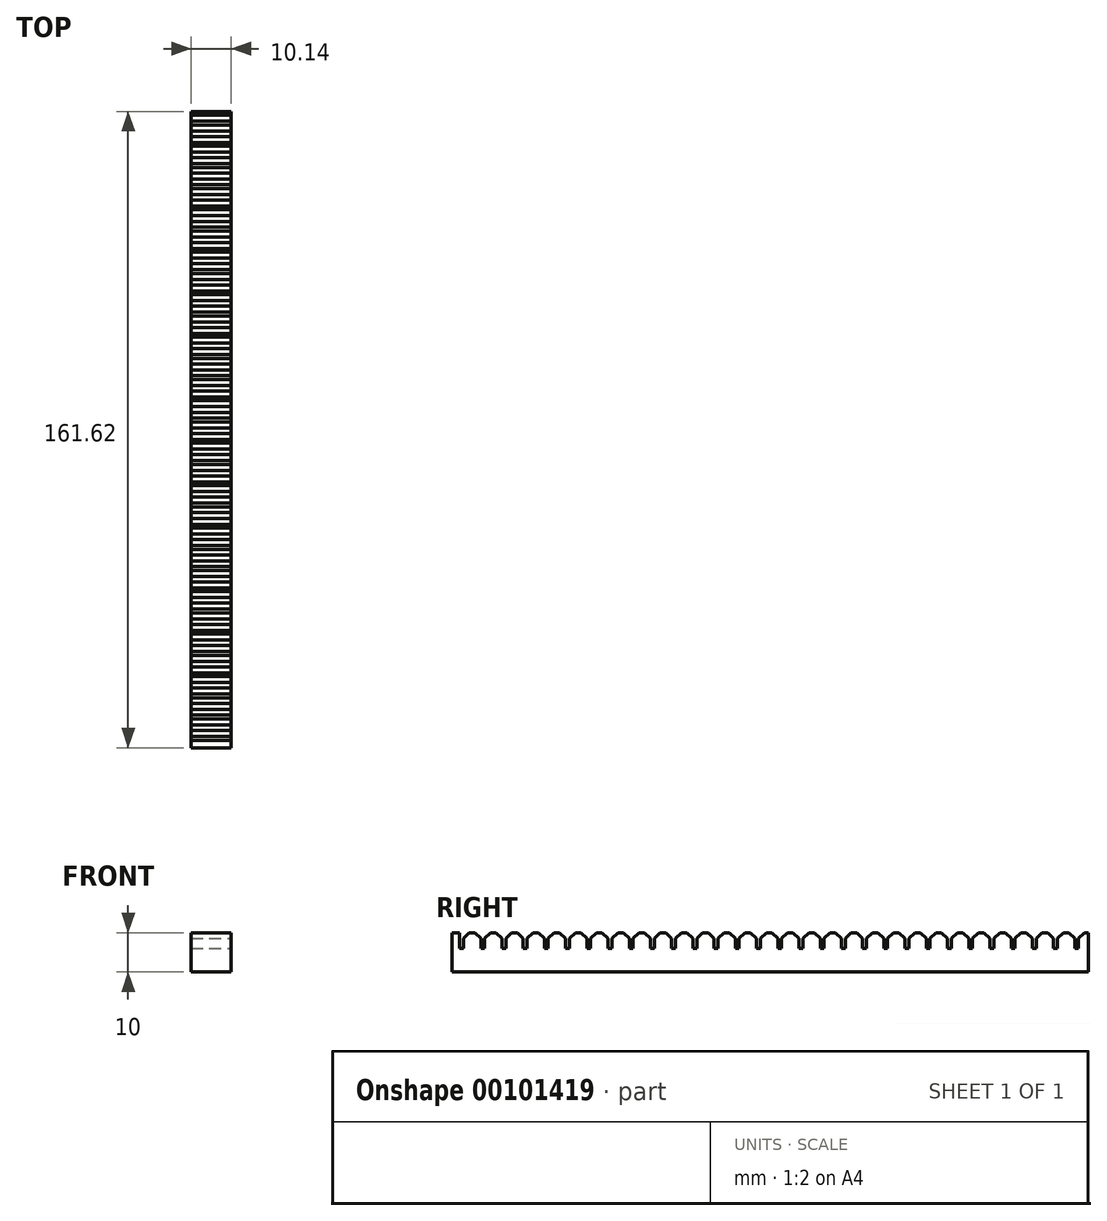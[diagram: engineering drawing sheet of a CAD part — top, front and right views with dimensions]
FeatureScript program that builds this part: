
annotation { "Feature Type Name" : "Feature", "Feature Type Description" : "" }
export const myFeature = defineFeature(function(context is Context, id is Id, definition is map)
    precondition{}
    {
        {
            var Q0;
            Q0=qCreatedBy(makeId("Top.planeOp"),FACE);
            var sketch = newSketch(context, id + "F0", { "sketchPlane" : qUnion([Q0])});
            skLineSegment(sketch, "E0.bottom", {"start": v(5.07, 80.81) * mm, "end": v(-5.07, 80.81) * mm});
            skLineSegment(sketch, "E0.top", {"start": v(5.07, -80.81) * mm, "end": v(-5.07, -80.81) * mm});
            skLineSegment(sketch, "E0.left", {"start": v(5.07, 80.81) * mm, "end": v(5.07, -80.81) * mm});
            skLineSegment(sketch, "E0.right", {"start": v(-5.07, 80.81) * mm, "end": v(-5.07, -80.81) * mm});
            skPoint(sketch, "E0.middle", {"position": v(0, 0) * mm});
            skSolve(sketch);
        }
        {
            var Q0;
            Q0=makeQuery(id+"F0.imprint","IMPRINT",FACE,{"disambiguationData":[TD([[makeQuery(id+"F0.imprint","IMPRINT",EDGE,{"derivedFrom":sQuery(id+"F0.wireOp",EDGE,"E0.bottom")}),1.0]])]});
            extrude(context, id + "F1", {"entities" : qUnion([Q0]), "depth" : 10 * mm});
        }
        {
            var Q0;
            Q0=makeQuery(id+"F1.opExtrude","CAP_FACE",FACE,{"disambiguationData":[OSD([sQuery(id+"F0.wireOp",EDGE,"E0.bottom"),sQuery(id+"F0.wireOp",EDGE,"E0.top"),sQuery(id+"F0.wireOp",EDGE,"E0.left"),sQuery(id+"F0.wireOp",EDGE,"E0.right")])],"isStart":false});
            var sketch = newSketch(context, id + "F2", { "sketchPlane" : qUnion([Q0])});
            skLineSegment(sketch, "E1.bottom", {"start": v(-5.07, -78.9) * mm, "end": v(5.07, -78.9) * mm});
            skLineSegment(sketch, "E1.top", {"start": v(-5.07, -77.94) * mm, "end": v(5.07, -77.94) * mm});
            skLineSegment(sketch, "E1.left", {"start": v(-5.07, -78.9) * mm, "end": v(-5.07, -77.94) * mm});
            skLineSegment(sketch, "E1.right", {"start": v(5.07, -78.9) * mm, "end": v(5.07, -77.94) * mm});
            skLineSegment(sketch, "E2.0.1.0", {"start": v(-5.07, -73.51) * mm, "end": v(5.07, -73.51) * mm});
            skLineSegment(sketch, "E2.0.1.1", {"start": v(-5.07, -72.55) * mm, "end": v(5.07, -72.55) * mm});
            skLineSegment(sketch, "E2.0.1.2", {"start": v(-5.07, -73.51) * mm, "end": v(-5.07, -72.55) * mm});
            skLineSegment(sketch, "E2.0.1.3", {"start": v(5.07, -73.51) * mm, "end": v(5.07, -72.55) * mm});
            skLineSegment(sketch, "E2.0.2.0", {"start": v(-5.07, -68.12) * mm, "end": v(5.07, -68.12) * mm});
            skLineSegment(sketch, "E2.0.2.1", {"start": v(-5.07, -67.16) * mm, "end": v(5.07, -67.16) * mm});
            skLineSegment(sketch, "E2.0.2.2", {"start": v(-5.07, -68.12) * mm, "end": v(-5.07, -67.16) * mm});
            skLineSegment(sketch, "E2.0.2.3", {"start": v(5.07, -68.12) * mm, "end": v(5.07, -67.16) * mm});
            skLineSegment(sketch, "E2.0.3.0", {"start": v(-5.07, -62.73) * mm, "end": v(5.07, -62.73) * mm});
            skLineSegment(sketch, "E2.0.3.1", {"start": v(-5.07, -61.77) * mm, "end": v(5.07, -61.77) * mm});
            skLineSegment(sketch, "E2.0.3.2", {"start": v(-5.07, -62.73) * mm, "end": v(-5.07, -61.77) * mm});
            skLineSegment(sketch, "E2.0.3.3", {"start": v(5.07, -62.73) * mm, "end": v(5.07, -61.77) * mm});
            skLineSegment(sketch, "E2.0.4.0", {"start": v(-5.07, -57.34) * mm, "end": v(5.07, -57.34) * mm});
            skLineSegment(sketch, "E2.0.4.1", {"start": v(-5.07, -56.38) * mm, "end": v(5.07, -56.38) * mm});
            skLineSegment(sketch, "E2.0.4.2", {"start": v(-5.07, -57.34) * mm, "end": v(-5.07, -56.38) * mm});
            skLineSegment(sketch, "E2.0.4.3", {"start": v(5.07, -57.34) * mm, "end": v(5.07, -56.38) * mm});
            skLineSegment(sketch, "E2.0.5.0", {"start": v(-5.07, -51.95) * mm, "end": v(5.07, -51.95) * mm});
            skLineSegment(sketch, "E2.0.5.1", {"start": v(-5.07, -50.99) * mm, "end": v(5.07, -50.99) * mm});
            skLineSegment(sketch, "E2.0.5.2", {"start": v(-5.07, -51.95) * mm, "end": v(-5.07, -50.99) * mm});
            skLineSegment(sketch, "E2.0.5.3", {"start": v(5.07, -51.95) * mm, "end": v(5.07, -50.99) * mm});
            skLineSegment(sketch, "E2.0.6.0", {"start": v(-5.07, -46.56) * mm, "end": v(5.07, -46.56) * mm});
            skLineSegment(sketch, "E2.0.6.1", {"start": v(-5.07, -45.6) * mm, "end": v(5.07, -45.6) * mm});
            skLineSegment(sketch, "E2.0.6.2", {"start": v(-5.07, -46.56) * mm, "end": v(-5.07, -45.6) * mm});
            skLineSegment(sketch, "E2.0.6.3", {"start": v(5.07, -46.56) * mm, "end": v(5.07, -45.6) * mm});
            skLineSegment(sketch, "E2.0.7.0", {"start": v(-5.07, -41.17) * mm, "end": v(5.07, -41.17) * mm});
            skLineSegment(sketch, "E2.0.7.1", {"start": v(-5.07, -40.2) * mm, "end": v(5.07, -40.2) * mm});
            skLineSegment(sketch, "E2.0.7.2", {"start": v(-5.07, -41.17) * mm, "end": v(-5.07, -40.2) * mm});
            skLineSegment(sketch, "E2.0.7.3", {"start": v(5.07, -41.17) * mm, "end": v(5.07, -40.2) * mm});
            skLineSegment(sketch, "E2.0.8.0", {"start": v(-5.07, -35.78) * mm, "end": v(5.07, -35.78) * mm});
            skLineSegment(sketch, "E2.0.8.1", {"start": v(-5.07, -34.82) * mm, "end": v(5.07, -34.82) * mm});
            skLineSegment(sketch, "E2.0.8.2", {"start": v(-5.07, -35.78) * mm, "end": v(-5.07, -34.82) * mm});
            skLineSegment(sketch, "E2.0.8.3", {"start": v(5.07, -35.78) * mm, "end": v(5.07, -34.82) * mm});
            skLineSegment(sketch, "E2.0.9.0", {"start": v(-5.07, -30.4) * mm, "end": v(5.07, -30.4) * mm});
            skLineSegment(sketch, "E2.0.9.1", {"start": v(-5.07, -29.43) * mm, "end": v(5.07, -29.43) * mm});
            skLineSegment(sketch, "E2.0.9.2", {"start": v(-5.07, -30.4) * mm, "end": v(-5.07, -29.43) * mm});
            skLineSegment(sketch, "E2.0.9.3", {"start": v(5.07, -30.4) * mm, "end": v(5.07, -29.43) * mm});
            skLineSegment(sketch, "E2.0.10.0", {"start": v(-5.07, -25) * mm, "end": v(5.07, -25) * mm});
            skLineSegment(sketch, "E2.0.10.1", {"start": v(-5.07, -24.04) * mm, "end": v(5.07, -24.04) * mm});
            skLineSegment(sketch, "E2.0.10.2", {"start": v(-5.07, -25) * mm, "end": v(-5.07, -24.04) * mm});
            skLineSegment(sketch, "E2.0.10.3", {"start": v(5.07, -25) * mm, "end": v(5.07, -24.04) * mm});
            skLineSegment(sketch, "E2.0.11.0", {"start": v(-5.07, -19.61) * mm, "end": v(5.07, -19.61) * mm});
            skLineSegment(sketch, "E2.0.11.1", {"start": v(-5.07, -18.65) * mm, "end": v(5.07, -18.65) * mm});
            skLineSegment(sketch, "E2.0.11.2", {"start": v(-5.07, -19.61) * mm, "end": v(-5.07, -18.65) * mm});
            skLineSegment(sketch, "E2.0.11.3", {"start": v(5.07, -19.61) * mm, "end": v(5.07, -18.65) * mm});
            skLineSegment(sketch, "E2.0.12.0", {"start": v(-5.07, -14.22) * mm, "end": v(5.07, -14.22) * mm});
            skLineSegment(sketch, "E2.0.12.1", {"start": v(-5.07, -13.26) * mm, "end": v(5.07, -13.26) * mm});
            skLineSegment(sketch, "E2.0.12.2", {"start": v(-5.07, -14.22) * mm, "end": v(-5.07, -13.26) * mm});
            skLineSegment(sketch, "E2.0.12.3", {"start": v(5.07, -14.22) * mm, "end": v(5.07, -13.26) * mm});
            skLineSegment(sketch, "E2.0.13.0", {"start": v(-5.07, -8.83) * mm, "end": v(5.07, -8.83) * mm});
            skLineSegment(sketch, "E2.0.13.1", {"start": v(-5.07, -7.87) * mm, "end": v(5.07, -7.87) * mm});
            skLineSegment(sketch, "E2.0.13.2", {"start": v(-5.07, -8.83) * mm, "end": v(-5.07, -7.87) * mm});
            skLineSegment(sketch, "E2.0.13.3", {"start": v(5.07, -8.83) * mm, "end": v(5.07, -7.87) * mm});
            skLineSegment(sketch, "E2.0.14.0", {"start": v(-5.07, -3.44) * mm, "end": v(5.07, -3.44) * mm});
            skLineSegment(sketch, "E2.0.14.1", {"start": v(-5.07, -2.48) * mm, "end": v(5.07, -2.48) * mm});
            skLineSegment(sketch, "E2.0.14.2", {"start": v(-5.07, -3.44) * mm, "end": v(-5.07, -2.48) * mm});
            skLineSegment(sketch, "E2.0.14.3", {"start": v(5.07, -3.44) * mm, "end": v(5.07, -2.48) * mm});
            skLineSegment(sketch, "E2.0.15.0", {"start": v(-5.07, 1.95) * mm, "end": v(5.07, 1.95) * mm});
            skLineSegment(sketch, "E2.0.15.1", {"start": v(-5.07, 2.91) * mm, "end": v(5.07, 2.91) * mm});
            skLineSegment(sketch, "E2.0.15.2", {"start": v(-5.07, 1.95) * mm, "end": v(-5.07, 2.91) * mm});
            skLineSegment(sketch, "E2.0.15.3", {"start": v(5.07, 1.95) * mm, "end": v(5.07, 2.91) * mm});
            skLineSegment(sketch, "E2.0.16.0", {"start": v(-5.07, 7.34) * mm, "end": v(5.07, 7.34) * mm});
            skLineSegment(sketch, "E2.0.16.1", {"start": v(-5.07, 8.3) * mm, "end": v(5.07, 8.3) * mm});
            skLineSegment(sketch, "E2.0.16.2", {"start": v(-5.07, 7.34) * mm, "end": v(-5.07, 8.3) * mm});
            skLineSegment(sketch, "E2.0.16.3", {"start": v(5.07, 7.34) * mm, "end": v(5.07, 8.3) * mm});
            skLineSegment(sketch, "E2.0.17.0", {"start": v(-5.07, 12.73) * mm, "end": v(5.07, 12.73) * mm});
            skLineSegment(sketch, "E2.0.17.1", {"start": v(-5.07, 13.7) * mm, "end": v(5.07, 13.7) * mm});
            skLineSegment(sketch, "E2.0.17.2", {"start": v(-5.07, 12.73) * mm, "end": v(-5.07, 13.7) * mm});
            skLineSegment(sketch, "E2.0.17.3", {"start": v(5.07, 12.73) * mm, "end": v(5.07, 13.7) * mm});
            skLineSegment(sketch, "E2.0.18.0", {"start": v(-5.07, 18.12) * mm, "end": v(5.07, 18.12) * mm});
            skLineSegment(sketch, "E2.0.18.1", {"start": v(-5.07, 19.08) * mm, "end": v(5.07, 19.08) * mm});
            skLineSegment(sketch, "E2.0.18.2", {"start": v(-5.07, 18.12) * mm, "end": v(-5.07, 19.08) * mm});
            skLineSegment(sketch, "E2.0.18.3", {"start": v(5.07, 18.12) * mm, "end": v(5.07, 19.08) * mm});
            skLineSegment(sketch, "E2.0.19.0", {"start": v(-5.07, 23.5) * mm, "end": v(5.07, 23.5) * mm});
            skLineSegment(sketch, "E2.0.19.1", {"start": v(-5.07, 24.47) * mm, "end": v(5.07, 24.47) * mm});
            skLineSegment(sketch, "E2.0.19.2", {"start": v(-5.07, 23.5) * mm, "end": v(-5.07, 24.47) * mm});
            skLineSegment(sketch, "E2.0.19.3", {"start": v(5.07, 23.5) * mm, "end": v(5.07, 24.47) * mm});
            skLineSegment(sketch, "E2.0.20.0", {"start": v(-5.07, 28.9) * mm, "end": v(5.07, 28.9) * mm});
            skLineSegment(sketch, "E2.0.20.1", {"start": v(-5.07, 29.86) * mm, "end": v(5.07, 29.86) * mm});
            skLineSegment(sketch, "E2.0.20.2", {"start": v(-5.07, 28.9) * mm, "end": v(-5.07, 29.86) * mm});
            skLineSegment(sketch, "E2.0.20.3", {"start": v(5.07, 28.9) * mm, "end": v(5.07, 29.86) * mm});
            skLineSegment(sketch, "E2.0.21.0", {"start": v(-5.07, 34.29) * mm, "end": v(5.07, 34.29) * mm});
            skLineSegment(sketch, "E2.0.21.1", {"start": v(-5.07, 35.25) * mm, "end": v(5.07, 35.25) * mm});
            skLineSegment(sketch, "E2.0.21.2", {"start": v(-5.07, 34.29) * mm, "end": v(-5.07, 35.25) * mm});
            skLineSegment(sketch, "E2.0.21.3", {"start": v(5.07, 34.29) * mm, "end": v(5.07, 35.25) * mm});
            skLineSegment(sketch, "E2.0.22.0", {"start": v(-5.07, 39.68) * mm, "end": v(5.07, 39.68) * mm});
            skLineSegment(sketch, "E2.0.22.1", {"start": v(-5.07, 40.64) * mm, "end": v(5.07, 40.64) * mm});
            skLineSegment(sketch, "E2.0.22.2", {"start": v(-5.07, 39.68) * mm, "end": v(-5.07, 40.64) * mm});
            skLineSegment(sketch, "E2.0.22.3", {"start": v(5.07, 39.68) * mm, "end": v(5.07, 40.64) * mm});
            skLineSegment(sketch, "E2.0.23.0", {"start": v(-5.07, 45.07) * mm, "end": v(5.07, 45.07) * mm});
            skLineSegment(sketch, "E2.0.23.1", {"start": v(-5.07, 46.03) * mm, "end": v(5.07, 46.03) * mm});
            skLineSegment(sketch, "E2.0.23.2", {"start": v(-5.07, 45.07) * mm, "end": v(-5.07, 46.03) * mm});
            skLineSegment(sketch, "E2.0.23.3", {"start": v(5.07, 45.07) * mm, "end": v(5.07, 46.03) * mm});
            skLineSegment(sketch, "E2.0.24.0", {"start": v(-5.07, 50.46) * mm, "end": v(5.07, 50.46) * mm});
            skLineSegment(sketch, "E2.0.24.1", {"start": v(-5.07, 51.42) * mm, "end": v(5.07, 51.42) * mm});
            skLineSegment(sketch, "E2.0.24.2", {"start": v(-5.07, 50.46) * mm, "end": v(-5.07, 51.42) * mm});
            skLineSegment(sketch, "E2.0.24.3", {"start": v(5.07, 50.46) * mm, "end": v(5.07, 51.42) * mm});
            skLineSegment(sketch, "E2.0.25.0", {"start": v(-5.07, 55.85) * mm, "end": v(5.07, 55.85) * mm});
            skLineSegment(sketch, "E2.0.25.1", {"start": v(-5.07, 56.81) * mm, "end": v(5.07, 56.81) * mm});
            skLineSegment(sketch, "E2.0.25.2", {"start": v(-5.07, 55.85) * mm, "end": v(-5.07, 56.81) * mm});
            skLineSegment(sketch, "E2.0.25.3", {"start": v(5.07, 55.85) * mm, "end": v(5.07, 56.81) * mm});
            skLineSegment(sketch, "E2.0.26.0", {"start": v(-5.07, 61.24) * mm, "end": v(5.07, 61.24) * mm});
            skLineSegment(sketch, "E2.0.26.1", {"start": v(-5.07, 62.2) * mm, "end": v(5.07, 62.2) * mm});
            skLineSegment(sketch, "E2.0.26.2", {"start": v(-5.07, 61.24) * mm, "end": v(-5.07, 62.2) * mm});
            skLineSegment(sketch, "E2.0.26.3", {"start": v(5.07, 61.24) * mm, "end": v(5.07, 62.2) * mm});
            skLineSegment(sketch, "E2.0.27.0", {"start": v(-5.07, 66.63) * mm, "end": v(5.07, 66.63) * mm});
            skLineSegment(sketch, "E2.0.27.1", {"start": v(-5.07, 67.6) * mm, "end": v(5.07, 67.6) * mm});
            skLineSegment(sketch, "E2.0.27.2", {"start": v(-5.07, 66.63) * mm, "end": v(-5.07, 67.6) * mm});
            skLineSegment(sketch, "E2.0.27.3", {"start": v(5.07, 66.63) * mm, "end": v(5.07, 67.6) * mm});
            skLineSegment(sketch, "E2.0.28.0", {"start": v(-5.07, 72.02) * mm, "end": v(5.07, 72.02) * mm});
            skLineSegment(sketch, "E2.0.28.1", {"start": v(-5.07, 72.98) * mm, "end": v(5.07, 72.98) * mm});
            skLineSegment(sketch, "E2.0.28.2", {"start": v(-5.07, 72.02) * mm, "end": v(-5.07, 72.98) * mm});
            skLineSegment(sketch, "E2.0.28.3", {"start": v(5.07, 72.02) * mm, "end": v(5.07, 72.98) * mm});
            skLineSegment(sketch, "E2.0.29.0", {"start": v(-5.07, 77.4) * mm, "end": v(5.07, 77.4) * mm});
            skLineSegment(sketch, "E2.0.29.1", {"start": v(-5.07, 78.37) * mm, "end": v(5.07, 78.37) * mm});
            skLineSegment(sketch, "E2.0.29.2", {"start": v(-5.07, 77.4) * mm, "end": v(-5.07, 78.37) * mm});
            skLineSegment(sketch, "E2.0.29.3", {"start": v(5.07, 77.4) * mm, "end": v(5.07, 78.37) * mm});
            skLineSegment(sketch, "E2.direction1", {"start": v(-5.07, -76.25) * mm, "end": v(19.93, -76.25) * mm, "construction": true});
            skLineSegment(sketch, "E2.direction2", {"start": v(-5.07, -78.9) * mm, "end": v(-5.07, -73.51) * mm, "construction": true});
            skSolve(sketch);
        }
        {
            var Q0;
            Q0=makeQuery(id+"F2.imprint","IMPRINT",FACE,{"disambiguationData":[TD([[makeQuery(id+"F2.imprint","IMPRINT",EDGE,{"derivedFrom":sQuery(id+"F2.wireOp",EDGE,"E1.bottom")}),1.0]])]});
            var Q1;
            Q1=makeQuery(id+"F2.imprint","IMPRINT",FACE,{"disambiguationData":[TD([[makeQuery(id+"F2.imprint","IMPRINT",EDGE,{"derivedFrom":sQuery(id+"F2.wireOp",EDGE,"E2.0.1.0")}),1.0]])]});
            var Q2;
            Q2=makeQuery(id+"F2.imprint","IMPRINT",FACE,{"disambiguationData":[TD([[makeQuery(id+"F2.imprint","IMPRINT",EDGE,{"derivedFrom":sQuery(id+"F2.wireOp",EDGE,"E2.0.2.0")}),1.0]])]});
            var Q3;
            Q3=makeQuery(id+"F2.imprint","IMPRINT",FACE,{"disambiguationData":[TD([[makeQuery(id+"F2.imprint","IMPRINT",EDGE,{"derivedFrom":sQuery(id+"F2.wireOp",EDGE,"E2.0.3.0")}),1.0]])]});
            var Q4;
            Q4=makeQuery(id+"F2.imprint","IMPRINT",FACE,{"disambiguationData":[TD([[makeQuery(id+"F2.imprint","IMPRINT",EDGE,{"derivedFrom":sQuery(id+"F2.wireOp",EDGE,"E2.0.4.0")}),1.0]])]});
            var Q5;
            Q5=makeQuery(id+"F2.imprint","IMPRINT",FACE,{"disambiguationData":[TD([[makeQuery(id+"F2.imprint","IMPRINT",EDGE,{"derivedFrom":sQuery(id+"F2.wireOp",EDGE,"E2.0.5.0")}),1.0]])]});
            var Q6;
            Q6=makeQuery(id+"F2.imprint","IMPRINT",FACE,{"disambiguationData":[TD([[makeQuery(id+"F2.imprint","IMPRINT",EDGE,{"derivedFrom":sQuery(id+"F2.wireOp",EDGE,"E2.0.6.0")}),1.0]])]});
            var Q7;
            Q7=makeQuery(id+"F2.imprint","IMPRINT",FACE,{"disambiguationData":[TD([[makeQuery(id+"F2.imprint","IMPRINT",EDGE,{"derivedFrom":sQuery(id+"F2.wireOp",EDGE,"E2.0.7.0")}),1.0]])]});
            var Q8;
            Q8=makeQuery(id+"F2.imprint","IMPRINT",FACE,{"disambiguationData":[TD([[makeQuery(id+"F2.imprint","IMPRINT",EDGE,{"derivedFrom":sQuery(id+"F2.wireOp",EDGE,"E2.0.8.0")}),1.0]])]});
            var Q9;
            Q9=makeQuery(id+"F2.imprint","IMPRINT",FACE,{"disambiguationData":[TD([[makeQuery(id+"F2.imprint","IMPRINT",EDGE,{"derivedFrom":sQuery(id+"F2.wireOp",EDGE,"E2.0.9.0")}),1.0]])]});
            var Q10;
            Q10=makeQuery(id+"F2.imprint","IMPRINT",FACE,{"disambiguationData":[TD([[makeQuery(id+"F2.imprint","IMPRINT",EDGE,{"derivedFrom":sQuery(id+"F2.wireOp",EDGE,"E2.0.10.0")}),1.0]])]});
            var Q11;
            Q11=makeQuery(id+"F2.imprint","IMPRINT",FACE,{"disambiguationData":[TD([[makeQuery(id+"F2.imprint","IMPRINT",EDGE,{"derivedFrom":sQuery(id+"F2.wireOp",EDGE,"E2.0.11.0")}),1.0]])]});
            var Q12;
            Q12=makeQuery(id+"F2.imprint","IMPRINT",FACE,{"disambiguationData":[TD([[makeQuery(id+"F2.imprint","IMPRINT",EDGE,{"derivedFrom":sQuery(id+"F2.wireOp",EDGE,"E2.0.12.0")}),1.0]])]});
            var Q13;
            Q13=makeQuery(id+"F2.imprint","IMPRINT",FACE,{"disambiguationData":[TD([[makeQuery(id+"F2.imprint","IMPRINT",EDGE,{"derivedFrom":sQuery(id+"F2.wireOp",EDGE,"E2.0.13.0")}),1.0]])]});
            var Q14;
            Q14=makeQuery(id+"F2.imprint","IMPRINT",FACE,{"disambiguationData":[TD([[makeQuery(id+"F2.imprint","IMPRINT",EDGE,{"derivedFrom":sQuery(id+"F2.wireOp",EDGE,"E2.0.14.0")}),1.0]])]});
            var Q15;
            Q15=makeQuery(id+"F2.imprint","IMPRINT",FACE,{"disambiguationData":[TD([[makeQuery(id+"F2.imprint","IMPRINT",EDGE,{"derivedFrom":sQuery(id+"F2.wireOp",EDGE,"E2.0.15.0")}),1.0]])]});
            var Q16;
            Q16=makeQuery(id+"F2.imprint","IMPRINT",FACE,{"disambiguationData":[TD([[makeQuery(id+"F2.imprint","IMPRINT",EDGE,{"derivedFrom":sQuery(id+"F2.wireOp",EDGE,"E2.0.16.0")}),1.0]])]});
            var Q17;
            Q17=makeQuery(id+"F2.imprint","IMPRINT",FACE,{"disambiguationData":[TD([[makeQuery(id+"F2.imprint","IMPRINT",EDGE,{"derivedFrom":sQuery(id+"F2.wireOp",EDGE,"E2.0.17.0")}),1.0]])]});
            var Q18;
            Q18=makeQuery(id+"F2.imprint","IMPRINT",FACE,{"disambiguationData":[TD([[makeQuery(id+"F2.imprint","IMPRINT",EDGE,{"derivedFrom":sQuery(id+"F2.wireOp",EDGE,"E2.0.18.0")}),1.0]])]});
            var Q19;
            Q19=makeQuery(id+"F2.imprint","IMPRINT",FACE,{"disambiguationData":[TD([[makeQuery(id+"F2.imprint","IMPRINT",EDGE,{"derivedFrom":sQuery(id+"F2.wireOp",EDGE,"E2.0.19.0")}),1.0]])]});
            var Q20;
            Q20=makeQuery(id+"F2.imprint","IMPRINT",FACE,{"disambiguationData":[TD([[makeQuery(id+"F2.imprint","IMPRINT",EDGE,{"derivedFrom":sQuery(id+"F2.wireOp",EDGE,"E2.0.20.0")}),1.0]])]});
            var Q21;
            Q21=makeQuery(id+"F2.imprint","IMPRINT",FACE,{"disambiguationData":[TD([[makeQuery(id+"F2.imprint","IMPRINT",EDGE,{"derivedFrom":sQuery(id+"F2.wireOp",EDGE,"E2.0.21.0")}),1.0]])]});
            var Q22;
            Q22=makeQuery(id+"F2.imprint","IMPRINT",FACE,{"disambiguationData":[TD([[makeQuery(id+"F2.imprint","IMPRINT",EDGE,{"derivedFrom":sQuery(id+"F2.wireOp",EDGE,"E2.0.22.0")}),1.0]])]});
            var Q23;
            Q23=makeQuery(id+"F2.imprint","IMPRINT",FACE,{"disambiguationData":[TD([[makeQuery(id+"F2.imprint","IMPRINT",EDGE,{"derivedFrom":sQuery(id+"F2.wireOp",EDGE,"E2.0.23.0")}),1.0]])]});
            var Q24;
            Q24=makeQuery(id+"F2.imprint","IMPRINT",FACE,{"disambiguationData":[TD([[makeQuery(id+"F2.imprint","IMPRINT",EDGE,{"derivedFrom":sQuery(id+"F2.wireOp",EDGE,"E2.0.24.0")}),1.0]])]});
            var Q25;
            Q25=makeQuery(id+"F2.imprint","IMPRINT",FACE,{"disambiguationData":[TD([[makeQuery(id+"F2.imprint","IMPRINT",EDGE,{"derivedFrom":sQuery(id+"F2.wireOp",EDGE,"E2.0.25.0")}),1.0]])]});
            var Q26;
            Q26=makeQuery(id+"F2.imprint","IMPRINT",FACE,{"disambiguationData":[TD([[makeQuery(id+"F2.imprint","IMPRINT",EDGE,{"derivedFrom":sQuery(id+"F2.wireOp",EDGE,"E2.0.26.0")}),1.0]])]});
            var Q27;
            Q27=makeQuery(id+"F2.imprint","IMPRINT",FACE,{"disambiguationData":[TD([[makeQuery(id+"F2.imprint","IMPRINT",EDGE,{"derivedFrom":sQuery(id+"F2.wireOp",EDGE,"E2.0.27.0")}),1.0]])]});
            var Q28;
            Q28=makeQuery(id+"F2.imprint","IMPRINT",FACE,{"disambiguationData":[TD([[makeQuery(id+"F2.imprint","IMPRINT",EDGE,{"derivedFrom":sQuery(id+"F2.wireOp",EDGE,"E2.0.28.0")}),1.0]])]});
            var Q29;
            Q29=makeQuery(id+"F2.imprint","IMPRINT",FACE,{"disambiguationData":[TD([[makeQuery(id+"F2.imprint","IMPRINT",EDGE,{"derivedFrom":sQuery(id+"F2.wireOp",EDGE,"E2.0.29.0")}),1.0]])]});
            extrude(context, id + "F3", {"entities" : qUnion([Q0, Q1, Q2, Q3, Q4, Q5, Q6, Q7, Q8, Q9, Q10, Q11, Q12, Q13, Q14, Q15, Q16, Q17, Q18, Q19, Q20, Q21, Q22, Q23, Q24, Q25, Q26, Q27, Q28, Q29]), "operationType" : NewBodyOperationType.REMOVE, "oppositeDirection" : true, "depth" : 4 * mm});
        }
        {
            var Q0;
            Q0=makeQuery(id+"F3.boolean.opBoolean","COPY",EDGE,{"derivedFrom":makeQuery(id+"F3.opExtrude","CAP_EDGE",EDGE,{"disambiguationData":[OSD([sQuery(id+"F2.wireOp",EDGE,"E2.0.5.1")])],"isStart":true})});
            var Q1;
            Q1=makeQuery(id+"F3.boolean.opBoolean","COPY",EDGE,{"derivedFrom":makeQuery(id+"F3.opExtrude","CAP_EDGE",EDGE,{"disambiguationData":[OSD([sQuery(id+"F2.wireOp",EDGE,"E2.0.5.0")])],"isStart":true})});
            var Q2;
            Q2=makeQuery(id+"F3.boolean.opBoolean","COPY",EDGE,{"derivedFrom":makeQuery(id+"F3.opExtrude","CAP_EDGE",EDGE,{"disambiguationData":[OSD([sQuery(id+"F2.wireOp",EDGE,"E2.0.4.0")])],"isStart":true})});
            var Q3;
            Q3=makeQuery(id+"F3.boolean.opBoolean","COPY",EDGE,{"derivedFrom":makeQuery(id+"F3.opExtrude","CAP_EDGE",EDGE,{"disambiguationData":[OSD([sQuery(id+"F2.wireOp",EDGE,"E2.0.4.1")])],"isStart":true})});
            var Q4;
            Q4=makeQuery(id+"F3.boolean.opBoolean","COPY",EDGE,{"derivedFrom":makeQuery(id+"F3.opExtrude","CAP_EDGE",EDGE,{"disambiguationData":[OSD([sQuery(id+"F2.wireOp",EDGE,"E2.0.3.1")])],"isStart":true})});
            var Q5;
            Q5=makeQuery(id+"F3.boolean.opBoolean","COPY",EDGE,{"derivedFrom":makeQuery(id+"F3.opExtrude","CAP_EDGE",EDGE,{"disambiguationData":[OSD([sQuery(id+"F2.wireOp",EDGE,"E2.0.3.0")])],"isStart":true})});
            var Q6;
            Q6=makeQuery(id+"F3.boolean.opBoolean","COPY",EDGE,{"derivedFrom":makeQuery(id+"F3.opExtrude","CAP_EDGE",EDGE,{"disambiguationData":[OSD([sQuery(id+"F2.wireOp",EDGE,"E2.0.2.1")])],"isStart":true})});
            var Q7;
            Q7=makeQuery(id+"F3.boolean.opBoolean","COPY",EDGE,{"derivedFrom":makeQuery(id+"F3.opExtrude","CAP_EDGE",EDGE,{"disambiguationData":[OSD([sQuery(id+"F2.wireOp",EDGE,"E2.0.2.0")])],"isStart":true})});
            var Q8;
            Q8=makeQuery(id+"F3.boolean.opBoolean","COPY",EDGE,{"derivedFrom":makeQuery(id+"F3.opExtrude","CAP_EDGE",EDGE,{"disambiguationData":[OSD([sQuery(id+"F2.wireOp",EDGE,"E2.0.1.1")])],"isStart":true})});
            var Q9;
            Q9=makeQuery(id+"F3.boolean.opBoolean","COPY",EDGE,{"derivedFrom":makeQuery(id+"F3.opExtrude","CAP_EDGE",EDGE,{"disambiguationData":[OSD([sQuery(id+"F2.wireOp",EDGE,"E2.0.1.0")])],"isStart":true})});
            var Q10;
            Q10=makeQuery(id+"F3.boolean.opBoolean","COPY",EDGE,{"derivedFrom":makeQuery(id+"F3.opExtrude","CAP_EDGE",EDGE,{"disambiguationData":[OSD([sQuery(id+"F2.wireOp",EDGE,"E1.top")])],"isStart":true})});
            var Q11;
            Q11=makeQuery(id+"F3.boolean.opBoolean","COPY",EDGE,{"derivedFrom":makeQuery(id+"F3.opExtrude","CAP_EDGE",EDGE,{"disambiguationData":[OSD([sQuery(id+"F2.wireOp",EDGE,"E1.bottom")])],"isStart":true})});
            var Q12;
            Q12=makeQuery(id+"F3.boolean.opBoolean","COPY",EDGE,{"derivedFrom":makeQuery(id+"F3.opExtrude","CAP_EDGE",EDGE,{"disambiguationData":[OSD([sQuery(id+"F2.wireOp",EDGE,"E2.0.6.0")])],"isStart":true})});
            var Q13;
            Q13=makeQuery(id+"F3.boolean.opBoolean","COPY",EDGE,{"derivedFrom":makeQuery(id+"F3.opExtrude","CAP_EDGE",EDGE,{"disambiguationData":[OSD([sQuery(id+"F2.wireOp",EDGE,"E2.0.6.1")])],"isStart":true})});
            var Q14;
            Q14=makeQuery(id+"F3.boolean.opBoolean","COPY",EDGE,{"derivedFrom":makeQuery(id+"F3.opExtrude","CAP_EDGE",EDGE,{"disambiguationData":[OSD([sQuery(id+"F2.wireOp",EDGE,"E2.0.7.0")])],"isStart":true})});
            var Q15;
            Q15=makeQuery(id+"F3.boolean.opBoolean","COPY",EDGE,{"derivedFrom":makeQuery(id+"F3.opExtrude","CAP_EDGE",EDGE,{"disambiguationData":[OSD([sQuery(id+"F2.wireOp",EDGE,"E2.0.7.1")])],"isStart":true})});
            var Q16;
            Q16=makeQuery(id+"F3.boolean.opBoolean","COPY",EDGE,{"derivedFrom":makeQuery(id+"F3.opExtrude","CAP_EDGE",EDGE,{"disambiguationData":[OSD([sQuery(id+"F2.wireOp",EDGE,"E2.0.8.0")])],"isStart":true})});
            var Q17;
            Q17=makeQuery(id+"F3.boolean.opBoolean","COPY",EDGE,{"derivedFrom":makeQuery(id+"F3.opExtrude","CAP_EDGE",EDGE,{"disambiguationData":[OSD([sQuery(id+"F2.wireOp",EDGE,"E2.0.8.1")])],"isStart":true})});
            var Q18;
            Q18=makeQuery(id+"F3.boolean.opBoolean","COPY",EDGE,{"derivedFrom":makeQuery(id+"F3.opExtrude","CAP_EDGE",EDGE,{"disambiguationData":[OSD([sQuery(id+"F2.wireOp",EDGE,"E2.0.9.0")])],"isStart":true})});
            var Q19;
            Q19=makeQuery(id+"F3.boolean.opBoolean","COPY",EDGE,{"derivedFrom":makeQuery(id+"F3.opExtrude","CAP_EDGE",EDGE,{"disambiguationData":[OSD([sQuery(id+"F2.wireOp",EDGE,"E2.0.10.0")])],"isStart":true})});
            var Q20;
            Q20=makeQuery(id+"F3.boolean.opBoolean","COPY",EDGE,{"derivedFrom":makeQuery(id+"F3.opExtrude","CAP_EDGE",EDGE,{"disambiguationData":[OSD([sQuery(id+"F2.wireOp",EDGE,"E2.0.10.1")])],"isStart":true})});
            var Q21;
            Q21=makeQuery(id+"F3.boolean.opBoolean","COPY",EDGE,{"derivedFrom":makeQuery(id+"F3.opExtrude","CAP_EDGE",EDGE,{"disambiguationData":[OSD([sQuery(id+"F2.wireOp",EDGE,"E2.0.11.0")])],"isStart":true})});
            var Q22;
            Q22=makeQuery(id+"F3.boolean.opBoolean","COPY",EDGE,{"derivedFrom":makeQuery(id+"F3.opExtrude","CAP_EDGE",EDGE,{"disambiguationData":[OSD([sQuery(id+"F2.wireOp",EDGE,"E2.0.11.1")])],"isStart":true})});
            var Q23;
            Q23=makeQuery(id+"F3.boolean.opBoolean","COPY",EDGE,{"derivedFrom":makeQuery(id+"F3.opExtrude","CAP_EDGE",EDGE,{"disambiguationData":[OSD([sQuery(id+"F2.wireOp",EDGE,"E2.0.12.0")])],"isStart":true})});
            var Q24;
            Q24=makeQuery(id+"F3.boolean.opBoolean","COPY",EDGE,{"derivedFrom":makeQuery(id+"F3.opExtrude","CAP_EDGE",EDGE,{"disambiguationData":[OSD([sQuery(id+"F2.wireOp",EDGE,"E2.0.12.1")])],"isStart":true})});
            var Q25;
            Q25=makeQuery(id+"F3.boolean.opBoolean","COPY",EDGE,{"derivedFrom":makeQuery(id+"F3.opExtrude","CAP_EDGE",EDGE,{"disambiguationData":[OSD([sQuery(id+"F2.wireOp",EDGE,"E2.0.13.0")])],"isStart":true})});
            var Q26;
            Q26=makeQuery(id+"F3.boolean.opBoolean","COPY",EDGE,{"derivedFrom":makeQuery(id+"F3.opExtrude","CAP_EDGE",EDGE,{"disambiguationData":[OSD([sQuery(id+"F2.wireOp",EDGE,"E2.0.13.1")])],"isStart":true})});
            var Q27;
            Q27=makeQuery(id+"F3.boolean.opBoolean","COPY",EDGE,{"derivedFrom":makeQuery(id+"F3.opExtrude","CAP_EDGE",EDGE,{"disambiguationData":[OSD([sQuery(id+"F2.wireOp",EDGE,"E2.0.14.0")])],"isStart":true})});
            var Q28;
            Q28=makeQuery(id+"F3.boolean.opBoolean","COPY",EDGE,{"derivedFrom":makeQuery(id+"F3.opExtrude","CAP_EDGE",EDGE,{"disambiguationData":[OSD([sQuery(id+"F2.wireOp",EDGE,"E2.0.14.1")])],"isStart":true})});
            var Q29;
            Q29=makeQuery(id+"F3.boolean.opBoolean","COPY",EDGE,{"derivedFrom":makeQuery(id+"F3.opExtrude","CAP_EDGE",EDGE,{"disambiguationData":[OSD([sQuery(id+"F2.wireOp",EDGE,"E2.0.15.0")])],"isStart":true})});
            var Q30;
            Q30=makeQuery(id+"F3.boolean.opBoolean","COPY",EDGE,{"derivedFrom":makeQuery(id+"F3.opExtrude","CAP_EDGE",EDGE,{"disambiguationData":[OSD([sQuery(id+"F2.wireOp",EDGE,"E2.0.15.1")])],"isStart":true})});
            var Q31;
            Q31=makeQuery(id+"F3.boolean.opBoolean","COPY",EDGE,{"derivedFrom":makeQuery(id+"F3.opExtrude","CAP_EDGE",EDGE,{"disambiguationData":[OSD([sQuery(id+"F2.wireOp",EDGE,"E2.0.16.0")])],"isStart":true})});
            var Q32;
            Q32=makeQuery(id+"F3.boolean.opBoolean","COPY",EDGE,{"derivedFrom":makeQuery(id+"F3.opExtrude","CAP_EDGE",EDGE,{"disambiguationData":[OSD([sQuery(id+"F2.wireOp",EDGE,"E2.0.16.1")])],"isStart":true})});
            var Q33;
            Q33=makeQuery(id+"F3.boolean.opBoolean","COPY",EDGE,{"derivedFrom":makeQuery(id+"F3.opExtrude","CAP_EDGE",EDGE,{"disambiguationData":[OSD([sQuery(id+"F2.wireOp",EDGE,"E2.0.17.0")])],"isStart":true})});
            var Q34;
            Q34=makeQuery(id+"F3.boolean.opBoolean","COPY",EDGE,{"derivedFrom":makeQuery(id+"F3.opExtrude","CAP_EDGE",EDGE,{"disambiguationData":[OSD([sQuery(id+"F2.wireOp",EDGE,"E2.0.17.1")])],"isStart":true})});
            var Q35;
            Q35=makeQuery(id+"F3.boolean.opBoolean","COPY",EDGE,{"derivedFrom":makeQuery(id+"F3.opExtrude","CAP_EDGE",EDGE,{"disambiguationData":[OSD([sQuery(id+"F2.wireOp",EDGE,"E2.0.18.0")])],"isStart":true})});
            var Q36;
            Q36=makeQuery(id+"F3.boolean.opBoolean","COPY",EDGE,{"derivedFrom":makeQuery(id+"F3.opExtrude","CAP_EDGE",EDGE,{"disambiguationData":[OSD([sQuery(id+"F2.wireOp",EDGE,"E2.0.18.1")])],"isStart":true})});
            var Q37;
            Q37=makeQuery(id+"F3.boolean.opBoolean","COPY",EDGE,{"derivedFrom":makeQuery(id+"F3.opExtrude","CAP_EDGE",EDGE,{"disambiguationData":[OSD([sQuery(id+"F2.wireOp",EDGE,"E2.0.19.0")])],"isStart":true})});
            var Q38;
            Q38=makeQuery(id+"F3.boolean.opBoolean","COPY",EDGE,{"derivedFrom":makeQuery(id+"F3.opExtrude","CAP_EDGE",EDGE,{"disambiguationData":[OSD([sQuery(id+"F2.wireOp",EDGE,"E2.0.20.1")])],"isStart":true})});
            var Q39;
            Q39=makeQuery(id+"F3.boolean.opBoolean","COPY",EDGE,{"derivedFrom":makeQuery(id+"F3.opExtrude","CAP_EDGE",EDGE,{"disambiguationData":[OSD([sQuery(id+"F2.wireOp",EDGE,"E2.0.20.0")])],"isStart":true})});
            var Q40;
            Q40=makeQuery(id+"F3.boolean.opBoolean","COPY",EDGE,{"derivedFrom":makeQuery(id+"F3.opExtrude","CAP_EDGE",EDGE,{"disambiguationData":[OSD([sQuery(id+"F2.wireOp",EDGE,"E2.0.19.1")])],"isStart":true})});
            var Q41;
            Q41=makeQuery(id+"F3.boolean.opBoolean","COPY",EDGE,{"derivedFrom":makeQuery(id+"F3.opExtrude","CAP_EDGE",EDGE,{"disambiguationData":[OSD([sQuery(id+"F2.wireOp",EDGE,"E2.0.21.0")])],"isStart":true})});
            var Q42;
            Q42=makeQuery(id+"F3.boolean.opBoolean","COPY",EDGE,{"derivedFrom":makeQuery(id+"F3.opExtrude","CAP_EDGE",EDGE,{"disambiguationData":[OSD([sQuery(id+"F2.wireOp",EDGE,"E2.0.21.1")])],"isStart":true})});
            var Q43;
            Q43=makeQuery(id+"F3.boolean.opBoolean","COPY",EDGE,{"derivedFrom":makeQuery(id+"F3.opExtrude","CAP_EDGE",EDGE,{"disambiguationData":[OSD([sQuery(id+"F2.wireOp",EDGE,"E2.0.22.0")])],"isStart":true})});
            var Q44;
            Q44=makeQuery(id+"F3.boolean.opBoolean","COPY",EDGE,{"derivedFrom":makeQuery(id+"F3.opExtrude","CAP_EDGE",EDGE,{"disambiguationData":[OSD([sQuery(id+"F2.wireOp",EDGE,"E2.0.22.1")])],"isStart":true})});
            var Q45;
            Q45=makeQuery(id+"F3.boolean.opBoolean","COPY",EDGE,{"derivedFrom":makeQuery(id+"F3.opExtrude","CAP_EDGE",EDGE,{"disambiguationData":[OSD([sQuery(id+"F2.wireOp",EDGE,"E2.0.23.0")])],"isStart":true})});
            var Q46;
            Q46=makeQuery(id+"F3.boolean.opBoolean","COPY",EDGE,{"derivedFrom":makeQuery(id+"F3.opExtrude","CAP_EDGE",EDGE,{"disambiguationData":[OSD([sQuery(id+"F2.wireOp",EDGE,"E2.0.23.1")])],"isStart":true})});
            var Q47;
            Q47=makeQuery(id+"F3.boolean.opBoolean","COPY",EDGE,{"derivedFrom":makeQuery(id+"F3.opExtrude","CAP_EDGE",EDGE,{"disambiguationData":[OSD([sQuery(id+"F2.wireOp",EDGE,"E2.0.24.0")])],"isStart":true})});
            var Q48;
            Q48=makeQuery(id+"F3.boolean.opBoolean","COPY",EDGE,{"derivedFrom":makeQuery(id+"F3.opExtrude","CAP_EDGE",EDGE,{"disambiguationData":[OSD([sQuery(id+"F2.wireOp",EDGE,"E2.0.29.1")])],"isStart":true})});
            var Q49;
            Q49=makeQuery(id+"F3.boolean.opBoolean","COPY",EDGE,{"derivedFrom":makeQuery(id+"F3.opExtrude","CAP_EDGE",EDGE,{"disambiguationData":[OSD([sQuery(id+"F2.wireOp",EDGE,"E2.0.29.0")])],"isStart":true})});
            var Q50;
            Q50=makeQuery(id+"F3.boolean.opBoolean","COPY",EDGE,{"derivedFrom":makeQuery(id+"F3.opExtrude","CAP_EDGE",EDGE,{"disambiguationData":[OSD([sQuery(id+"F2.wireOp",EDGE,"E2.0.28.1")])],"isStart":true})});
            var Q51;
            Q51=makeQuery(id+"F3.boolean.opBoolean","COPY",EDGE,{"derivedFrom":makeQuery(id+"F3.opExtrude","CAP_EDGE",EDGE,{"disambiguationData":[OSD([sQuery(id+"F2.wireOp",EDGE,"E2.0.28.0")])],"isStart":true})});
            var Q52;
            Q52=makeQuery(id+"F3.boolean.opBoolean","COPY",EDGE,{"derivedFrom":makeQuery(id+"F3.opExtrude","CAP_EDGE",EDGE,{"disambiguationData":[OSD([sQuery(id+"F2.wireOp",EDGE,"E2.0.27.1")])],"isStart":true})});
            var Q53;
            Q53=makeQuery(id+"F3.boolean.opBoolean","COPY",EDGE,{"derivedFrom":makeQuery(id+"F3.opExtrude","CAP_EDGE",EDGE,{"disambiguationData":[OSD([sQuery(id+"F2.wireOp",EDGE,"E2.0.27.0")])],"isStart":true})});
            var Q54;
            Q54=makeQuery(id+"F3.boolean.opBoolean","COPY",EDGE,{"derivedFrom":makeQuery(id+"F3.opExtrude","CAP_EDGE",EDGE,{"disambiguationData":[OSD([sQuery(id+"F2.wireOp",EDGE,"E2.0.26.1")])],"isStart":true})});
            var Q55;
            Q55=makeQuery(id+"F3.boolean.opBoolean","COPY",EDGE,{"derivedFrom":makeQuery(id+"F3.opExtrude","CAP_EDGE",EDGE,{"disambiguationData":[OSD([sQuery(id+"F2.wireOp",EDGE,"E2.0.26.0")])],"isStart":true})});
            var Q56;
            Q56=makeQuery(id+"F3.boolean.opBoolean","COPY",EDGE,{"derivedFrom":makeQuery(id+"F3.opExtrude","CAP_EDGE",EDGE,{"disambiguationData":[OSD([sQuery(id+"F2.wireOp",EDGE,"E2.0.25.1")])],"isStart":true})});
            var Q57;
            Q57=makeQuery(id+"F3.boolean.opBoolean","COPY",EDGE,{"derivedFrom":makeQuery(id+"F3.opExtrude","CAP_EDGE",EDGE,{"disambiguationData":[OSD([sQuery(id+"F2.wireOp",EDGE,"E2.0.25.0")])],"isStart":true})});
            var Q58;
            Q58=makeQuery(id+"F3.boolean.opBoolean","COPY",EDGE,{"derivedFrom":makeQuery(id+"F3.opExtrude","CAP_EDGE",EDGE,{"disambiguationData":[OSD([sQuery(id+"F2.wireOp",EDGE,"E2.0.24.1")])],"isStart":true})});
            var Q59;
            Q59=makeQuery(id+"F3.boolean.opBoolean","COPY",EDGE,{"derivedFrom":makeQuery(id+"F3.opExtrude","CAP_EDGE",EDGE,{"disambiguationData":[OSD([sQuery(id+"F2.wireOp",EDGE,"E2.0.9.1")])],"isStart":true})});
            chamfer(context, id + "F4", {"entities" : qUnion([Q0, Q1, Q2, Q3, Q4, Q5, Q6, Q7, Q8, Q9, Q10, Q11, Q12, Q13, Q14, Q15, Q16, Q17, Q18, Q19, Q20, Q21, Q22, Q23, Q24, Q25, Q26, Q27, Q28, Q29, Q30, Q31, Q32, Q33, Q34, Q35, Q36, Q37, Q38, Q39, Q40, Q41, Q42, Q43, Q44, Q45, Q46, Q47, Q48, Q49, Q50, Q51, Q52, Q53, Q54, Q55, Q56, Q57, Q58, Q59]), "width" : 1.5 * mm, "tangentPropagation" : true});
        }
    });
